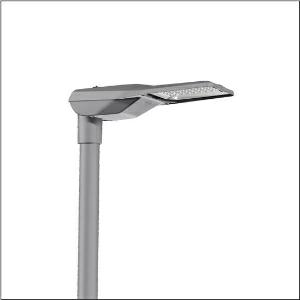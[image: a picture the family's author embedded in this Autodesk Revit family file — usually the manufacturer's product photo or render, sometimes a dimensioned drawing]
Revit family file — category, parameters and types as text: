
# Revit family: streetlight_sl_21_iq_mini___st1_0ab_5xe2m31v08hb_1211
name_source: partatom
category: Lighting Fixtures
units: mm (PartAtom-declared; Revit-internal decimal feet)

## family parameters
Cut with Voids When Loaded = No
Host = Face
Light Source = No
Part Type = Normal
Room Calculation Point = No
Round Connector Dimension = Use Diameter
Shared = No

## types (1)
- --- (1 x LED, 8580 lm, 71 W, 3000K)
    Apparent Load = 71 VA
    CIE Flux Codes = 38 73 97 100 100
    Color Rendering = 70
    Color Temperature = 3000K
    Default Elevation = 1800 mm
    Description = Streetlight SL 21 iQ mini, mast luminaire, primary light control with lens, of PMMA, primary optical cover: cover, of toughened safety glass, transparent, light distribution: ST1.0aB, light emission: direct distribution, primary light characteristic: asymmetric, installation type: post-top, side-entry, LED, High Power LED, rated luminous flux: 8.580lm, luminous efficacy: 121lm/W, light colour: 730, colour temperature: 3000K, control: presetting dimming logarithmic, Street-Remote, Auto-Match, Temp-Guard, Lumen-Switch, Night-Set, Smart-Wire, Light-Fading, Desk-Remote (wireless, voltage-free reading and setting of iQ features in the workshop via application-optimized NFC function/RFID function), optimised constant luminous flux control (CLO 2.0), mains connection: 220..240V, AC, 50/60Hz, start of lifetime: 71W, end of service life: 75W, reduction: 30W, luminaire housing, of diecast aluminium, powder-coated, Siteco® metallic grey (DB 702S), corrosivity category C5 mid according to DIN EN ISO 12944, please order mast flange separately, inclination adjustable: 0°, 5°, 10°, 15°, sealing non-destructively replaceable, multi-level sealing system, length: 628mm, width: 235mm, height: 110mm, mast flange for spigot size: 42mm (side-entry): 5XC10008XM4, 60/48mm (side-entry/post-top): 5XC10108XM2, 76/60mm (side-entry/post-top): 5XC10108XM1, Smart Interface above, protection rating (complete): IP66, insulation class (complete): insulation class II (safety insulation), certification: CE, ENEC, ENEC+, VDE, impact resistance: IK09, permissible operating ambient temperature for outdoor applications: -40..+50°C, standard-compliant lighting for roads and squares, packaging unit: 1 piece

Light Distribution: ST1.0aB
    Height = 110 mm
    Lamp = 1 x LED
    Lamp Light Flux = 8580 lm
    Lamp Power = 71 W
    Lamp count = 1
    Length = 625 mm
    Luminous efficacy = 121 lm/W
    Manufacturer = Siteco
    ModVariant = No
    Model = 5XE2M31V08HB
    Number of Poles = 1
    OnlyDefault = Yes
    Power Factor = 1
    Product Name = Streetlight SL 21 iQ mini | ST1.0aB
    Product group = mast luminaire | pylon top
    ProductGroupID = 6100
    Protection Class = Protection class II
    Protection Degree = IP 66
    RLX_Detail_Level = 1
    RLX_Emergency_Light_Flux = 0 lm
    RLX_Emergency_Type = 0
    RLX_Emergency_Type_DB = No
    RlxData = <blob elided: 92521 chars, md5=1eb532d9>
    Socket = socket
    Standby Power = 0 W
    System Light Flux = 8580 lm
    System Power = 71 W
    Type Comments = factory setting: luminous flux: 100 % | dim-lin: 254 | 716 mA
    Type Image = l_1003515.jpg
    URL = http://relux.com
    VarID = @adj_042561
    Voltage = 0 V
    Weight = 0.00 kg
    Width = 234 mm

## geometry (parser evidence)
native form markers: Blend x4, Sweep x10
no freeform markers — native parametric forms only
